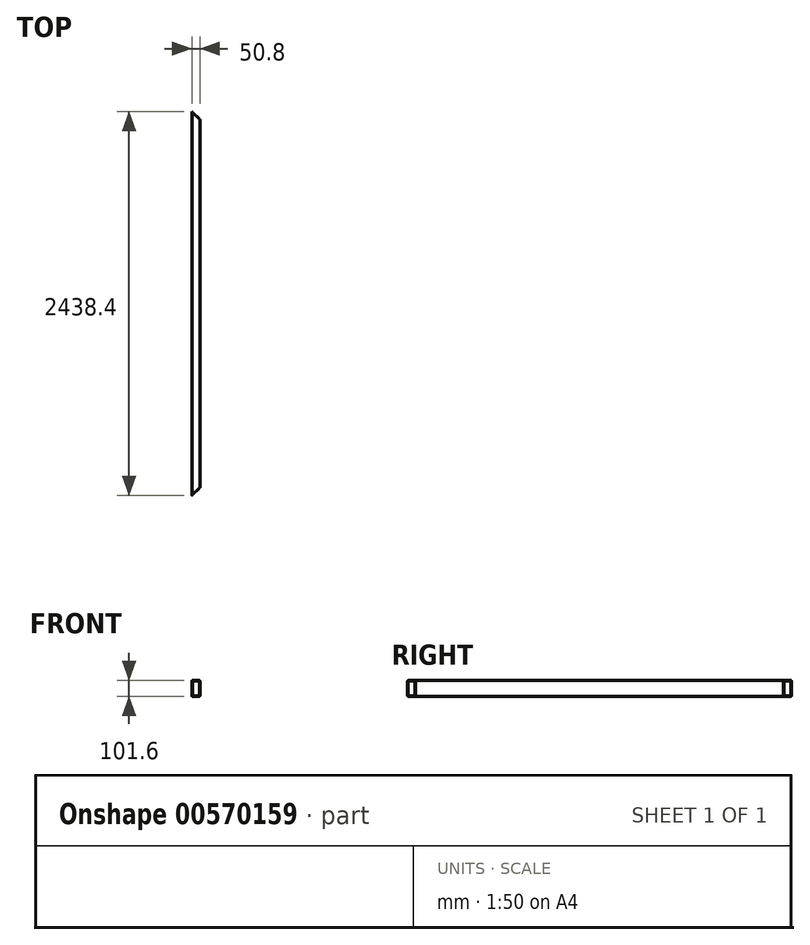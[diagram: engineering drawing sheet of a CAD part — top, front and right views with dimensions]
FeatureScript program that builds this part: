
annotation { "Feature Type Name" : "Feature", "Feature Type Description" : "" }
export const myFeature = defineFeature(function(context is Context, id is Id, definition is map)
    precondition{}
    {
        {
            var Q0;
            Q0=qCreatedBy(makeId("Front.planeOp"),FACE);
            var sketch = newSketch(context, id + "F0", { "sketchPlane" : qUnion([Q0])});
            skLineSegment(sketch, "E0.bottom", {"start": v(0, 0) * mm, "end": v(50.8, 0) * mm});
            skLineSegment(sketch, "E0.top", {"start": v(0, 101.6) * mm, "end": v(50.8, 101.6) * mm});
            skLineSegment(sketch, "E0.left", {"start": v(0, 0) * mm, "end": v(0, 101.6) * mm});
            skLineSegment(sketch, "E0.right", {"start": v(50.8, 0) * mm, "end": v(50.8, 101.6) * mm});
            skLineSegment(sketch, "E1.bottom", {"start": v(3.18, 3.18) * mm, "end": v(47.63, 3.18) * mm});
            skLineSegment(sketch, "E1.top", {"start": v(3.17, 98.43) * mm, "end": v(47.62, 98.43) * mm});
            skLineSegment(sketch, "E1.left", {"start": v(3.17, 3.18) * mm, "end": v(3.17, 98.43) * mm});
            skLineSegment(sketch, "E1.right", {"start": v(47.63, 3.17) * mm, "end": v(47.62, 98.43) * mm});
            skSolve(sketch);
        }
        {
            var Q0;
            Q0=makeQuery(id+"F0.imprint","IMPRINT",FACE,{"disambiguationData":[TD([[makeQuery(id+"F0.imprint","IMPRINT",EDGE,{"derivedFrom":sQuery(id+"F0.wireOp",EDGE,"E0.bottom")}),1.0]])]});
            extrude(context, id + "F1", {"entities" : qUnion([Q0]), "depth" : 2438.4 * mm, "offsetDistance" : 25.4 * mm});
        }
        {
            var Q0;
            Q0=makeQuery(id+"F1.opExtrude","SWEPT_FACE",FACE,{"disambiguationData":[OSD([sQuery(id+"F0.wireOp",EDGE,"E0.top")])]});
            var sketch = newSketch(context, id + "F2", { "sketchPlane" : qUnion([Q0])});
            skLineSegment(sketch, "E2", {"start": v(0, 0) * mm, "end": v(50.8, -50.8) * mm});
            skLineSegment(sketch, "E3", {"start": v(0, -2438.4) * mm, "end": v(50.8, -2387.6) * mm});
            skSolve(sketch);
        }
        {
            var Q0;
            {var subQ0=sQuery(id+"F2.wireOp",EDGE,"E2");Q0=makeQuery(id+"F2.imprint","IMPRINT",FACE,{"disambiguationData":[TD([[makeQuery(id+"F2.imprint","IMPRINT",EDGE,{"derivedFrom":subQ0}),1.0]])]});}
            var Q1;
            {var subQ0=sQuery(id+"F2.wireOp",EDGE,"E3");Q1=makeQuery(id+"F2.imprint","IMPRINT",FACE,{"disambiguationData":[TD([[makeQuery(id+"F2.imprint","IMPRINT",EDGE,{"derivedFrom":subQ0}),-1.0]])]});}
            extrude(context, id + "F3", {"entities" : qUnion([Q0, Q1]), "operationType" : NewBodyOperationType.REMOVE, "oppositeDirection" : true, "depth" : 135.38 * mm, "offsetDistance" : 25.4 * mm});
        }
        {
            var Q0;
            Q0=makeQuery(id+"F1.opExtrude","SWEPT_EDGE",EDGE,{"disambiguationData":[OSD([sQuery(id+"F0.wireOp",EDGE,"E0.top"),sQuery(id+"F0.wireOp",EDGE,"E0.right")])]});
            var Q1;
            Q1=makeQuery(id+"F1.opExtrude","SWEPT_EDGE",EDGE,{"disambiguationData":[OSD([sQuery(id+"F0.wireOp",EDGE,"E0.top"),sQuery(id+"F0.wireOp",EDGE,"E0.left")])]});
            var Q2;
            Q2=makeQuery(id+"F1.opExtrude","SWEPT_EDGE",EDGE,{"disambiguationData":[OSD([sQuery(id+"F0.wireOp",EDGE,"E0.bottom"),sQuery(id+"F0.wireOp",EDGE,"E0.right")])]});
            var Q3;
            Q3=makeQuery(id+"F1.opExtrude","SWEPT_EDGE",EDGE,{"disambiguationData":[OSD([sQuery(id+"F0.wireOp",EDGE,"E0.bottom"),sQuery(id+"F0.wireOp",EDGE,"E0.left")])]});
            fillet(context, id + "F4", {"entities" : qUnion([Q0, Q1, Q2, Q3]), "radius" : 5.08 * mm, "tangentPropagation" : true, "allowEdgeOverflow" : false});
        }
    });
